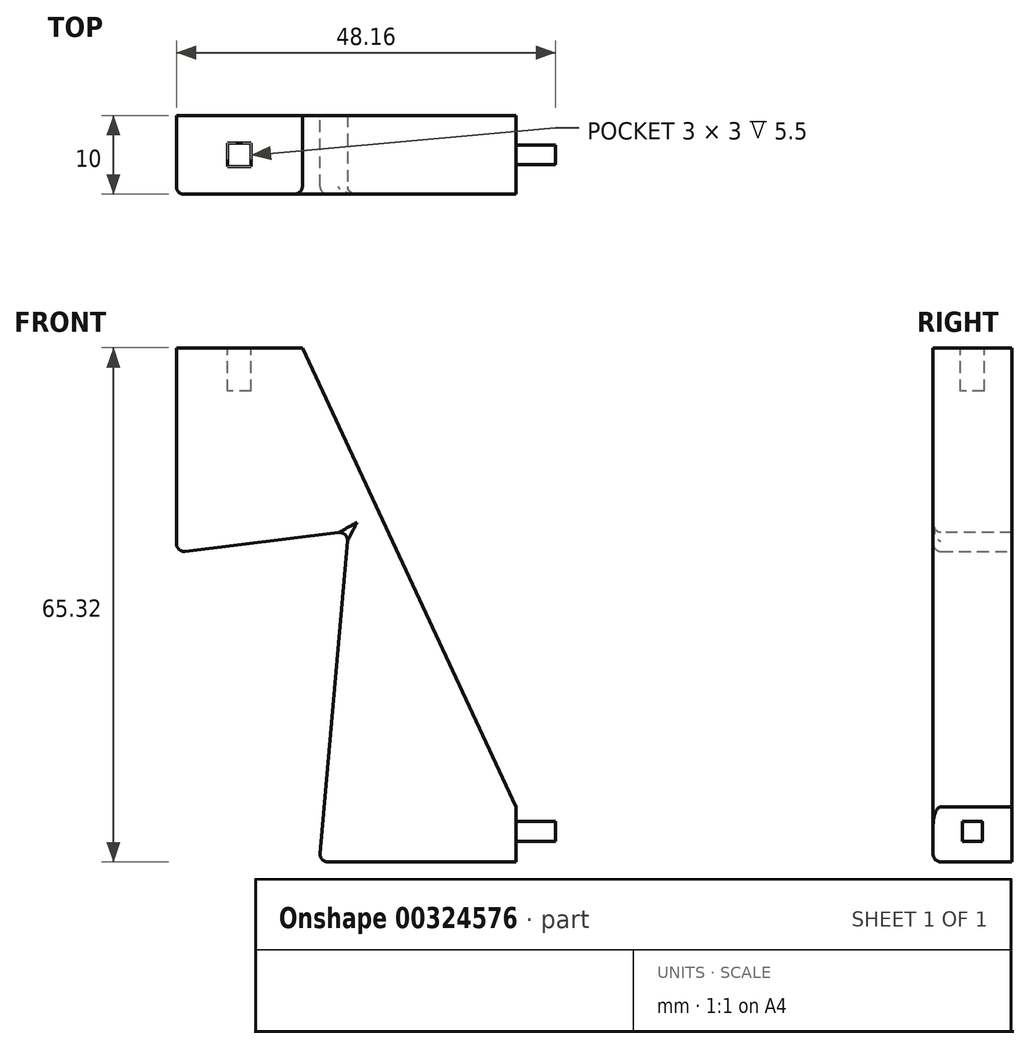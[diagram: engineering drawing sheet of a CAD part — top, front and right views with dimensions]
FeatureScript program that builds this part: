
annotation { "Feature Type Name" : "Feature", "Feature Type Description" : "" }
export const myFeature = defineFeature(function(context is Context, id is Id, definition is map)
    precondition{}
    {
        {
            var Q0;
            Q0=qCreatedBy(makeId("Front.planeOp"),FACE);
            var sketch = newSketch(context, id + "F0", { "sketchPlane" : qUnion([Q0])});
            skLineSegment(sketch, "E0", {"start": v(0, 0) * mm, "end": v(0, 7) * mm});
            skLineSegment(sketch, "E1", {"start": v(0, 0) * mm, "end": v(-25, 0) * mm});
            skLineSegment(sketch, "E2", {"start": v(-25, 0) * mm, "end": v(-21.33, 42) * mm});
            skLineSegment(sketch, "E3", {"start": v(-21.33, 42) * mm, "end": v(-43.16, 39.32) * mm});
            skLineSegment(sketch, "E4", {"start": v(-43.16, 39.32) * mm, "end": v(-43.16, 65.32) * mm});
            skLineSegment(sketch, "E5", {"start": v(-43.16, 65.32) * mm, "end": v(-27.16, 65.32) * mm});
            skLineSegment(sketch, "E6", {"start": v(-27.16, 65.32) * mm, "end": v(0, 7) * mm});
            skSolve(sketch);
        }
        {
            var Q0;
            Q0=makeQuery(id+"F0.imprint","IMPRINT",FACE,{"disambiguationData":[TD([[makeQuery(id+"F0.imprint","IMPRINT",EDGE,{"derivedFrom":sQuery(id+"F0.wireOp",EDGE,"E0")}),1.0]])]});
            extrude(context, id + "F1", {"entities" : qUnion([Q0]), "depth" : 10 * mm});
        }
        {
            var Q0;
            Q0=makeQuery(id+"F1.opExtrude","CAP_EDGE",EDGE,{"disambiguationData":[OSD([sQuery(id+"F0.wireOp",EDGE,"E3")])],"isStart":false});
            fillet(context, id + "F2", {"entities" : qUnion([Q0]), "radius" : 1 * mm, "tangentPropagation" : true, "allowEdgeOverflow" : false});
        }
        {
            var Q0;
            Q0=makeQuery(id+"F1.opExtrude","SWEPT_FACE",FACE,{"disambiguationData":[OSD([sQuery(id+"F0.wireOp",EDGE,"E0")])]});
            var sketch = newSketch(context, id + "F3", { "sketchPlane" : qUnion([Q0])});
            skLineSegment(sketch, "E7.bottom", {"start": v(-3.75, 5.13) * mm, "end": v(-6.25, 5.13) * mm});
            skLineSegment(sketch, "E7.top", {"start": v(-3.75, 2.63) * mm, "end": v(-6.25, 2.63) * mm});
            skLineSegment(sketch, "E7.left", {"start": v(-3.75, 5.13) * mm, "end": v(-3.75, 2.63) * mm});
            skLineSegment(sketch, "E7.right", {"start": v(-6.25, 5.13) * mm, "end": v(-6.25, 2.63) * mm});
            skPoint(sketch, "E7.middle", {"position": v(-5, 3.88) * mm});
            skSolve(sketch);
        }
        {
            var Q0;
            Q0 = qSketchRegion(id + "F3", true);
            extrude(context, id + "F4", {"entities" : qUnion([Q0]), "operationType" : NewBodyOperationType.ADD, "depth" : 5 * mm});
        }
        {
            var Q0;
            Q0=makeQuery(id+"F1.opExtrude","SWEPT_FACE",FACE,{"disambiguationData":[OSD([sQuery(id+"F0.wireOp",EDGE,"E5")])]});
            var sketch = newSketch(context, id + "F5", { "sketchPlane" : qUnion([Q0])});
            skLineSegment(sketch, "E8.bottom", {"start": v(-33.66, -3.5) * mm, "end": v(-36.66, -3.5) * mm});
            skLineSegment(sketch, "E8.top", {"start": v(-33.66, -6.5) * mm, "end": v(-36.66, -6.5) * mm});
            skLineSegment(sketch, "E8.left", {"start": v(-33.66, -3.5) * mm, "end": v(-33.66, -6.5) * mm});
            skLineSegment(sketch, "E8.right", {"start": v(-36.66, -3.5) * mm, "end": v(-36.66, -6.5) * mm});
            skSolve(sketch);
        }
        {
            var Q0;
            Q0=makeQuery(id+"F5.imprint","IMPRINT",FACE,{"disambiguationData":[TD([[makeQuery(id+"F5.imprint","IMPRINT",EDGE,{"derivedFrom":sQuery(id+"F5.wireOp",EDGE,"E8.bottom")}),1.0]])]});
            extrude(context, id + "F6", {"entities" : qUnion([Q0]), "operationType" : NewBodyOperationType.REMOVE, "oppositeDirection" : true, "depth" : 5.5 * mm});
        }
        {
            var Q0;
            Q0=makeQuery(id+"F1.opExtrude","SWEPT_EDGE",EDGE,{"disambiguationData":[OSD([sQuery(id+"F0.wireOp",EDGE,"E3"),sQuery(id+"F0.wireOp",EDGE,"E4")])]});
            var Q1;
            Q1=makeQuery(id+"F1.opExtrude","CAP_EDGE",EDGE,{"disambiguationData":[OSD([sQuery(id+"F0.wireOp",EDGE,"E2")])],"isStart":false});
            fillet(context, id + "F7", {"entities" : qUnion([Q0, Q1]), "radius" : 1 * mm, "tangentPropagation" : true, "allowEdgeOverflow" : false});
        }
        {
            var Q0;
            Q0=makeQuery(id+"F1.opExtrude","CAP_EDGE",EDGE,{"disambiguationData":[OSD([sQuery(id+"F0.wireOp",EDGE,"E1")])],"isStart":false});
            var Q1;
            Q1=makeQuery(id+"F1.opExtrude","CAP_EDGE",EDGE,{"disambiguationData":[OSD([sQuery(id+"F0.wireOp",EDGE,"E6")])],"isStart":false});
            fillet(context, id + "F8", {"entities" : qUnion([Q0, Q1]), "radius" : 1 * mm, "tangentPropagation" : true, "allowEdgeOverflow" : false});
        }
        {
            var Q0;
            Q0=makeQuery(id+"F1.opExtrude","SWEPT_EDGE",EDGE,{"disambiguationData":[OSD([sQuery(id+"F0.wireOp",EDGE,"E2"),sQuery(id+"F0.wireOp",EDGE,"E3")])]});
            fillet(context, id + "F9", {"entities" : qUnion([Q0]), "radius" : 1 * mm, "tangentPropagation" : true, "allowEdgeOverflow" : false});
        }
    });
